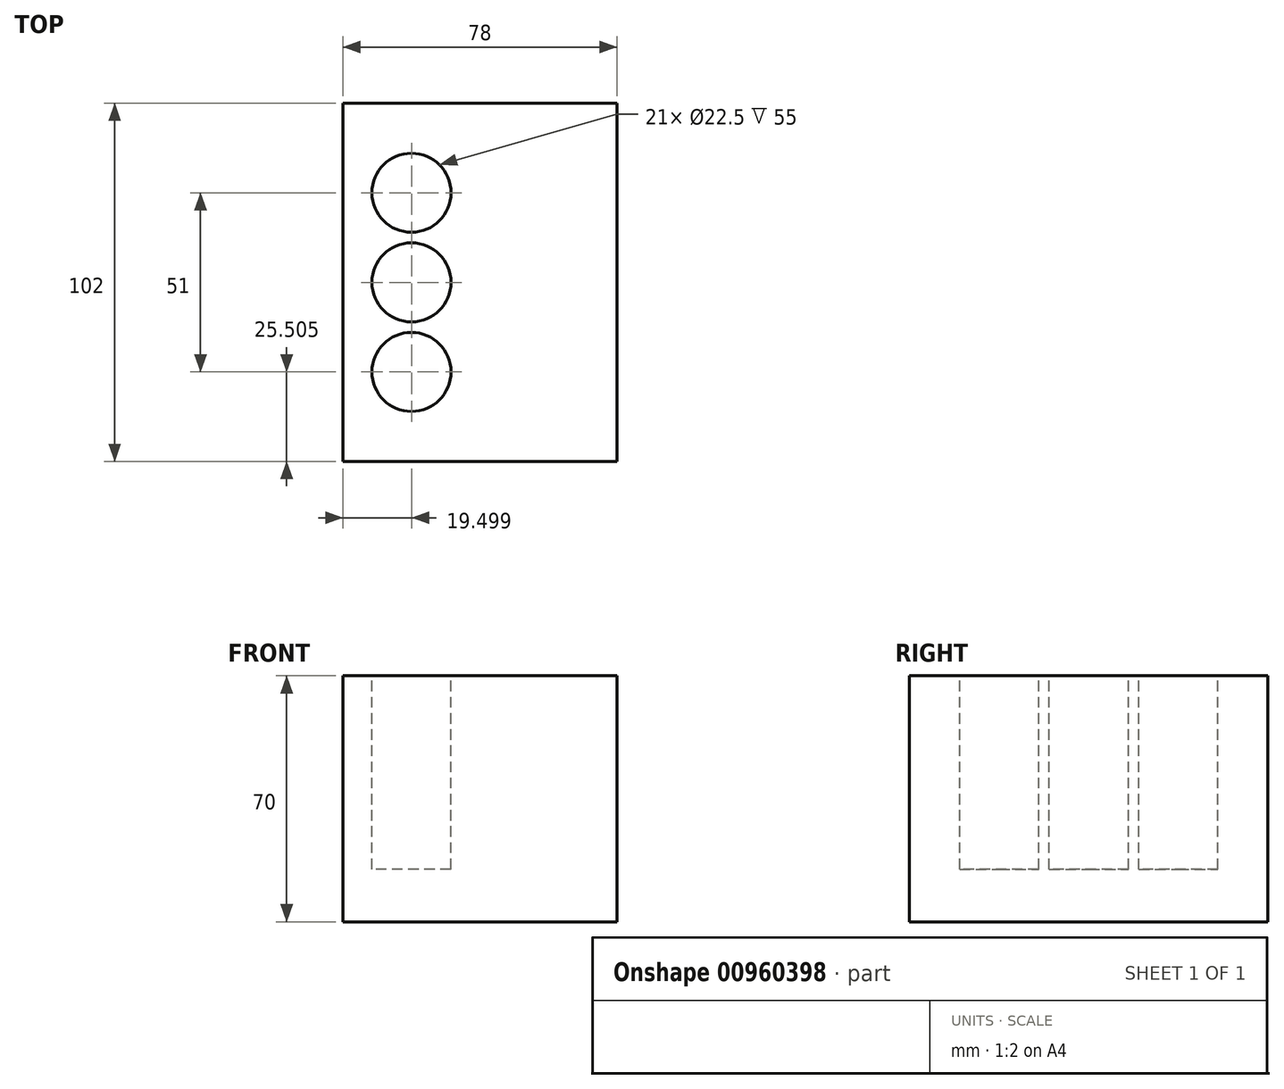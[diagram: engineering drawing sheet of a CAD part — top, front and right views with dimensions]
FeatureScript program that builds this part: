
annotation { "Feature Type Name" : "Feature", "Feature Type Description" : "" }
export const myFeature = defineFeature(function(context is Context, id is Id, definition is map)
    precondition{}
    {
        {
            var Q0;
            Q0=qCreatedBy(makeId("Top.planeOp"),FACE);
            var sketch = newSketch(context, id + "F0", { "sketchPlane" : qUnion([Q0])});
            skLineSegment(sketch, "E0.bottom", {"start": v(-31.51, 124.58) * mm, "end": v(46.49, 124.58) * mm});
            skLineSegment(sketch, "E0.top", {"start": v(-31.51, 22.58) * mm, "end": v(46.49, 22.58) * mm});
            skLineSegment(sketch, "E0.left", {"start": v(-31.51, 124.58) * mm, "end": v(-31.51, 22.58) * mm});
            skLineSegment(sketch, "E0.right", {"start": v(46.49, 124.58) * mm, "end": v(46.49, 22.58) * mm});
            skSolve(sketch);
        }
        {
            var Q0;
            Q0=makeQuery(id+"F0.imprint","IMPRINT",FACE,{"disambiguationData":[TD([[makeQuery(id+"F0.imprint","IMPRINT",EDGE,{"derivedFrom":sQuery(id+"F0.wireOp",EDGE,"E0.bottom")}),-1.0]])]});
            extrude(context, id + "F1", {"entities" : qUnion([Q0]), "depth" : 70 * mm, "offsetDistance" : 25 * mm});
        }
        {
            var Q0;
            Q0=makeQuery(id+"F1.opExtrude","CAP_FACE",FACE,{"disambiguationData":[OSD([sQuery(id+"F0.wireOp",EDGE,"E0.bottom"),sQuery(id+"F0.wireOp",EDGE,"E0.top"),sQuery(id+"F0.wireOp",EDGE,"E0.left"),sQuery(id+"F0.wireOp",EDGE,"E0.right")])],"isStart":false});
            var sketch = newSketch(context, id + "F2", { "sketchPlane" : qUnion([Q0])});
            skPoint(sketch, "E1", {"position": v(7.49, 22.58) * mm});
            skPoint(sketch, "E2", {"position": v(-31.51, 73.58) * mm});
            skPoint(sketch, "E3", {"position": v(46.49, 73.58) * mm});
            skPoint(sketch, "E4", {"position": v(7.49, 124.58) * mm});
            skPoint(sketch, "E5", {"position": v(7.49, 73.58) * mm});
            skPoint(sketch, "E6", {"position": v(-12.01, 22.58) * mm});
            skPoint(sketch, "E7", {"position": v(29.1, 22.58) * mm});
            skPoint(sketch, "E8", {"position": v(46.49, 48.08) * mm});
            skPoint(sketch, "E9", {"position": v(46.49, 99.08) * mm});
            skPoint(sketch, "E10", {"position": v(-31.51, 99.08) * mm});
            skPoint(sketch, "E11", {"position": v(-31.51, 48.08) * mm});
            skPoint(sketch, "E12", {"position": v(-12.01, 48.08) * mm});
            skPoint(sketch, "E13", {"position": v(29.1, 48.08) * mm});
            skPoint(sketch, "E14", {"position": v(29.1, 99.08) * mm});
            skPoint(sketch, "E15", {"position": v(-12.01, 99.08) * mm});
            skPoint(sketch, "E16", {"position": v(29.1, 73.58) * mm});
            skPoint(sketch, "E17", {"position": v(-12.01, 73.58) * mm});
            skCircle(sketch, "E18", {"center": v(-12.01, 99.08) * mm, "radius": 11.25 * mm});
            skCircle(sketch, "E19", {"center": v(-12.01, 73.58) * mm, "radius": 11.25 * mm});
            skCircle(sketch, "E20", {"center": v(-12.01, 48.08) * mm, "radius": 11.25 * mm});
            skPoint(sketch, "E21", {"position": v(29.1, 112.77) * mm});
            skPoint(sketch, "E22", {"position": v(-12.01, 36.83) * mm});
            skPoint(sketch, "E23", {"position": v(-12.01, 110.33) * mm});
            skSolve(sketch);
        }
        {
            var Q0;
            Q0=makeQuery(id+"F2.imprint","IMPRINT",FACE,{"disambiguationData":[TD([[makeQuery(id+"F2.imprint","IMPRINT",EDGE,{"derivedFrom":sQuery(id+"F2.wireOp",EDGE,"E18")}),1.0]])]});
            var Q1;
            Q1=makeQuery(id+"F2.imprint","IMPRINT",FACE,{"disambiguationData":[TD([[makeQuery(id+"F2.imprint","IMPRINT",EDGE,{"derivedFrom":sQuery(id+"F2.wireOp",EDGE,"E19")}),1.0]])]});
            var Q2;
            Q2=makeQuery(id+"F2.imprint","IMPRINT",FACE,{"disambiguationData":[TD([[makeQuery(id+"F2.imprint","IMPRINT",EDGE,{"derivedFrom":sQuery(id+"F2.wireOp",EDGE,"E20")}),1.0]])]});
            extrude(context, id + "F3", {"entities" : qUnion([Q0, Q1, Q2]), "operationType" : NewBodyOperationType.REMOVE, "oppositeDirection" : true, "depth" : 55 * mm, "offsetDistance" : 25 * mm});
        }
    });
